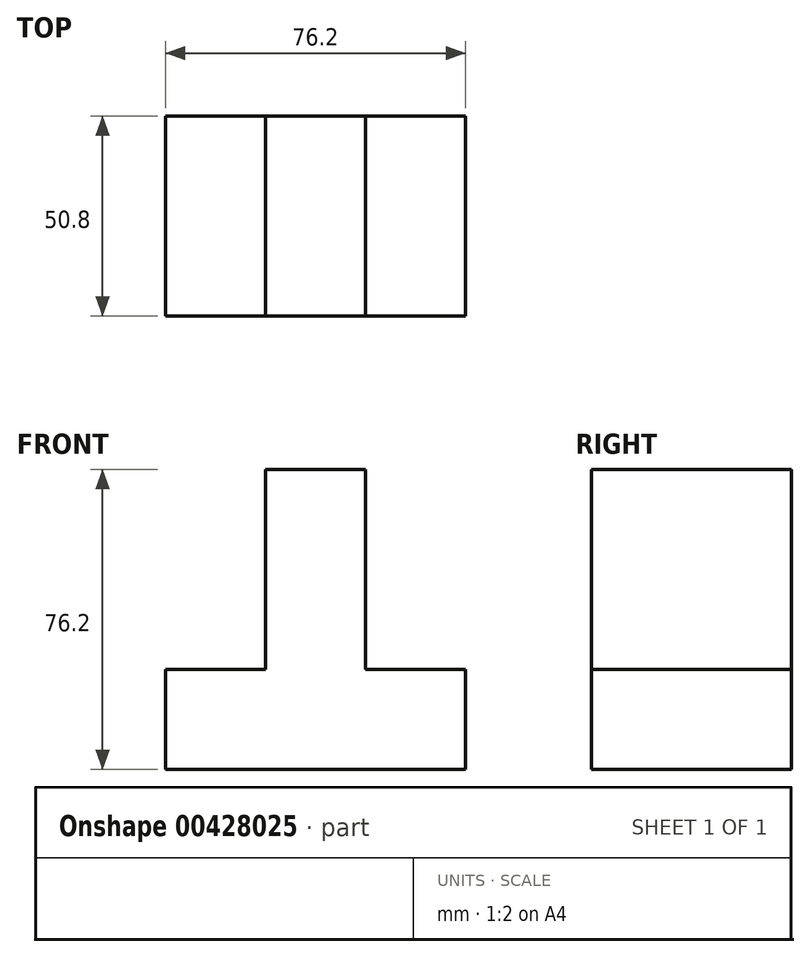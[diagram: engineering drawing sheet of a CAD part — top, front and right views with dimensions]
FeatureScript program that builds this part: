
annotation { "Feature Type Name" : "Feature", "Feature Type Description" : "" }
export const myFeature = defineFeature(function(context is Context, id is Id, definition is map)
    precondition{}
    {
        {
            var Q0;
            Q0=qCreatedBy(makeId("Front.planeOp"),FACE);
            var sketch = newSketch(context, id + "F0", { "sketchPlane" : qUnion([Q0])});
            skLineSegment(sketch, "E0", {"start": v(-76.2, 0) * mm, "end": v(-76.2, 25.4) * mm});
            skLineSegment(sketch, "E1", {"start": v(-76.2, 25.4) * mm, "end": v(-50.8, 25.4) * mm});
            skLineSegment(sketch, "E2", {"start": v(-50.8, 25.4) * mm, "end": v(-50.8, 76.2) * mm});
            skLineSegment(sketch, "E3", {"start": v(-50.8, 76.2) * mm, "end": v(-25.4, 76.2) * mm});
            skLineSegment(sketch, "E4", {"start": v(-25.4, 76.2) * mm, "end": v(-25.4, 25.4) * mm});
            skLineSegment(sketch, "E5", {"start": v(-25.4, 25.4) * mm, "end": v(0, 25.4) * mm});
            skLineSegment(sketch, "E6", {"start": v(0, 25.4) * mm, "end": v(0, 0) * mm});
            skLineSegment(sketch, "E7", {"start": v(0, 0) * mm, "end": v(-76.2, 0) * mm});
            skSolve(sketch);
        }
        {
            var Q0;
            Q0 = qSketchRegion(id + "F0", true);
            extrude(context, id + "F1", {"entities" : qUnion([Q0]), "depth" : 50.8 * mm});
        }
    });
